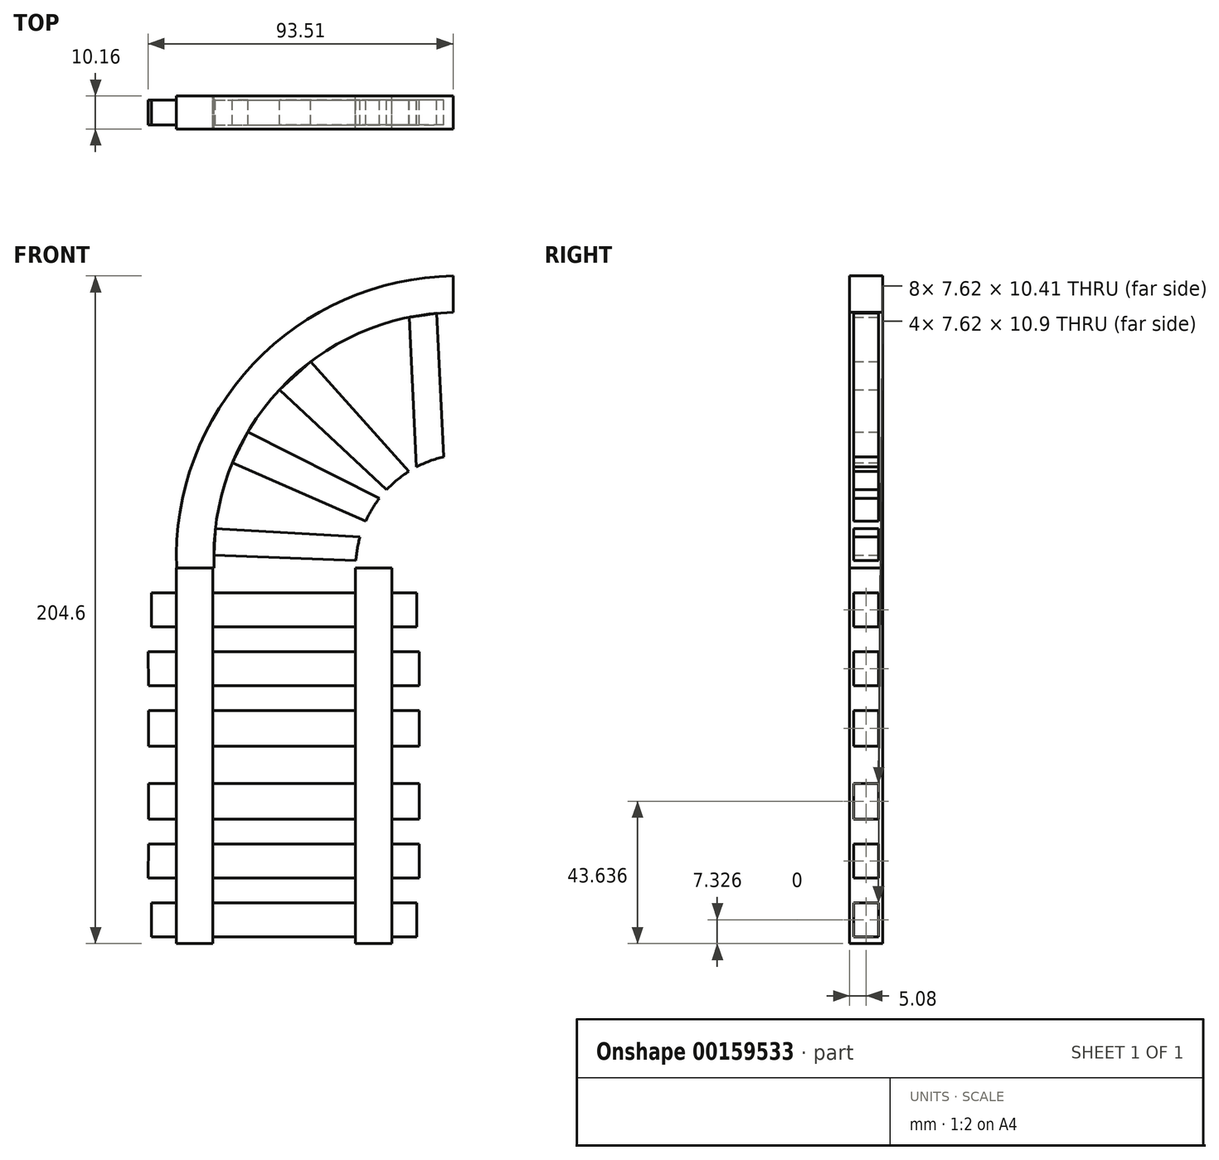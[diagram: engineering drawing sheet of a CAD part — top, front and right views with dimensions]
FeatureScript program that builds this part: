
annotation { "Feature Type Name" : "Feature", "Feature Type Description" : "" }
export const myFeature = defineFeature(function(context is Context, id is Id, definition is map)
    precondition{}
    {
        {
            var Q0;
            Q0=qCreatedBy(makeId("Front.planeOp"),FACE);
            var sketch = newSketch(context, id + "F0", { "sketchPlane" : qUnion([Q0])});
            skLineSegment(sketch, "E0", {"start": v(-21.84, 60.28) * mm, "end": v(-21.84, -54.78) * mm});
            skLineSegment(sketch, "E1", {"start": v(-21.84, -54.78) * mm, "end": v(-33.02, -54.78) * mm});
            skLineSegment(sketch, "E2", {"start": v(-33.02, -54.78) * mm, "end": v(-33.02, 60.28) * mm});
            skLineSegment(sketch, "E3", {"start": v(-33.02, 60.28) * mm, "end": v(-21.84, 60.28) * mm});
            skLineSegment(sketch, "E4.MirrorCS", {"start": v(21.84, 60.28) * mm, "end": v(21.84, -54.78) * mm});
            skLineSegment(sketch, "E5.MirrorCS", {"start": v(33.02, -54.78) * mm, "end": v(33.02, 60.28) * mm});
            skLineSegment(sketch, "E6.MirrorCS", {"start": v(33.02, 60.28) * mm, "end": v(21.84, 60.28) * mm});
            skLineSegment(sketch, "E7.MirrorCS", {"start": v(21.84, -54.78) * mm, "end": v(33.02, -54.78) * mm});
            skLineSegment(sketch, "E8", {"start": v(-40.64, 42.25) * mm, "end": v(40.64, 42.25) * mm});
            skLineSegment(sketch, "E9", {"start": v(40.64, 42.25) * mm, "end": v(40.64, 52.66) * mm});
            skLineSegment(sketch, "E10", {"start": v(40.64, 52.66) * mm, "end": v(-40.64, 52.66) * mm});
            skLineSegment(sketch, "E11", {"start": v(-40.64, 52.66) * mm, "end": v(-40.64, 42.25) * mm});
            skLineSegment(sketch, "E12", {"start": v(-41.74, 34.63) * mm, "end": v(41.35, 34.63) * mm});
            skLineSegment(sketch, "E13", {"start": v(41.35, 34.63) * mm, "end": v(41.35, 24.21) * mm});
            skLineSegment(sketch, "E14", {"start": v(41.35, 24.21) * mm, "end": v(-41.51, 24.21) * mm});
            skLineSegment(sketch, "E15", {"start": v(-41.51, 24.21) * mm, "end": v(-41.74, 34.63) * mm});
            skLineSegment(sketch, "E16", {"start": v(-33.02, 16.6) * mm, "end": v(-41.51, 16.6) * mm});
            skLineSegment(sketch, "E17", {"start": v(-41.51, 16.6) * mm, "end": v(-41.51, 5.7) * mm});
            skLineSegment(sketch, "E18", {"start": v(-41.51, 5.7) * mm, "end": v(41.4, 5.7) * mm});
            skLineSegment(sketch, "E19", {"start": v(41.4, 5.7) * mm, "end": v(41.4, 16.6) * mm});
            skLineSegment(sketch, "E20", {"start": v(-33.02, 16.6) * mm, "end": v(41.4, 16.6) * mm});
            skLineSegment(sketch, "E21.MirrorCS", {"start": v(-41.51, -5.7) * mm, "end": v(41.4, -5.7) * mm});
            skLineSegment(sketch, "E22.MirrorCS", {"start": v(-41.51, -16.6) * mm, "end": v(-41.51, -5.7) * mm});
            skLineSegment(sketch, "E23.MirrorCS", {"start": v(41.4, -5.7) * mm, "end": v(41.4, -16.6) * mm});
            skLineSegment(sketch, "E24.MirrorCS", {"start": v(-33.02, -16.6) * mm, "end": v(41.4, -16.6) * mm});
            skLineSegment(sketch, "E25.MirrorCS", {"start": v(-33.02, -16.6) * mm, "end": v(-41.51, -16.6) * mm});
            skLineSegment(sketch, "E26.MirrorCS", {"start": v(41.35, -24.21) * mm, "end": v(-41.51, -24.21) * mm});
            skLineSegment(sketch, "E27.MirrorCS", {"start": v(-41.74, -34.63) * mm, "end": v(41.35, -34.63) * mm});
            skLineSegment(sketch, "E28.MirrorCS", {"start": v(-41.51, -24.21) * mm, "end": v(-41.74, -34.63) * mm});
            skLineSegment(sketch, "E29.MirrorCS", {"start": v(41.35, -34.63) * mm, "end": v(41.35, -24.21) * mm});
            skLineSegment(sketch, "E30.MirrorCS", {"start": v(40.64, -42.25) * mm, "end": v(40.64, -52.66) * mm});
            skLineSegment(sketch, "E31.MirrorCS", {"start": v(40.64, -52.66) * mm, "end": v(-40.64, -52.66) * mm});
            skLineSegment(sketch, "E32.MirrorCS", {"start": v(-40.64, -42.25) * mm, "end": v(40.64, -42.25) * mm});
            skLineSegment(sketch, "E33.MirrorCS", {"start": v(-40.64, -52.66) * mm, "end": v(-40.64, -42.25) * mm});
            skSolve(sketch);
        }
        {
            var Q0;
            {var subQ0=sQuery(id+"F0.wireOp",EDGE,"E3");Q0=makeQuery(id+"F0.imprint","IMPRINT",FACE,{"disambiguationData":[TD([[makeQuery(id+"F0.imprint","IMPRINT",EDGE,{"derivedFrom":subQ0}),-1.0]])]});}
            var Q1;
            {var subQ0=sQuery(id+"F0.wireOp",EDGE,"E10");var subQ1=sQuery(id+"F0.wireOp",EDGE,"E0");var subQ2=makeQuery(id+"F0.imprint","INTERSECT",VERTEX,{"derivedFrom":[subQ1,subQ0]});Q1=makeQuery(id+"F0.imprint","IMPRINT",FACE,{"disambiguationData":[TD([[makeQuery(id+"F0.imprint","IMPRINT",EDGE,{"disambiguationData":[TD([[subQ2,-1.0]])],"derivedFrom":subQ1}),-1.0]])]});}
            var Q2;
            {var subQ0=sQuery(id+"F0.wireOp",EDGE,"E8");var subQ1=sQuery(id+"F0.wireOp",EDGE,"E0");var subQ2=makeQuery(id+"F0.imprint","INTERSECT",VERTEX,{"derivedFrom":[subQ1,subQ0]});Q2=makeQuery(id+"F0.imprint","IMPRINT",FACE,{"disambiguationData":[TD([[makeQuery(id+"F0.imprint","IMPRINT",EDGE,{"disambiguationData":[TD([[subQ2,-1.0]])],"derivedFrom":subQ1}),-1.0]])]});}
            var Q3;
            {var subQ0=sQuery(id+"F0.wireOp",EDGE,"E12");var subQ1=sQuery(id+"F0.wireOp",EDGE,"E0");var subQ2=makeQuery(id+"F0.imprint","INTERSECT",VERTEX,{"derivedFrom":[subQ1,subQ0]});Q3=makeQuery(id+"F0.imprint","IMPRINT",FACE,{"disambiguationData":[TD([[makeQuery(id+"F0.imprint","IMPRINT",EDGE,{"disambiguationData":[TD([[subQ2,-1.0]])],"derivedFrom":subQ1}),-1.0]])]});}
            var Q4;
            {var subQ0=sQuery(id+"F0.wireOp",EDGE,"E14");var subQ1=sQuery(id+"F0.wireOp",EDGE,"E0");var subQ2=makeQuery(id+"F0.imprint","INTERSECT",VERTEX,{"derivedFrom":[subQ1,subQ0]});Q4=makeQuery(id+"F0.imprint","IMPRINT",FACE,{"disambiguationData":[TD([[makeQuery(id+"F0.imprint","IMPRINT",EDGE,{"disambiguationData":[TD([[subQ2,-1.0]])],"derivedFrom":subQ1}),-1.0]])]});}
            var Q5;
            {var subQ0=sQuery(id+"F0.wireOp",EDGE,"E20");var subQ1=sQuery(id+"F0.wireOp",EDGE,"E0");var subQ2=makeQuery(id+"F0.imprint","INTERSECT",VERTEX,{"derivedFrom":[subQ1,subQ0]});Q5=makeQuery(id+"F0.imprint","IMPRINT",FACE,{"disambiguationData":[TD([[makeQuery(id+"F0.imprint","IMPRINT",EDGE,{"disambiguationData":[TD([[subQ2,-1.0]])],"derivedFrom":subQ1}),-1.0]])]});}
            var Q6;
            {var subQ0=sQuery(id+"F0.wireOp",EDGE,"E18");var subQ1=sQuery(id+"F0.wireOp",EDGE,"E0");var subQ2=makeQuery(id+"F0.imprint","INTERSECT",VERTEX,{"derivedFrom":[subQ1,subQ0]});Q6=makeQuery(id+"F0.imprint","IMPRINT",FACE,{"disambiguationData":[TD([[makeQuery(id+"F0.imprint","IMPRINT",EDGE,{"disambiguationData":[TD([[subQ2,-1.0]])],"derivedFrom":subQ1}),-1.0]])]});}
            var Q7;
            {var subQ0=sQuery(id+"F0.wireOp",EDGE,"E21.MirrorCS");var subQ1=sQuery(id+"F0.wireOp",EDGE,"E0");var subQ2=makeQuery(id+"F0.imprint","INTERSECT",VERTEX,{"derivedFrom":[subQ1,subQ0]});Q7=makeQuery(id+"F0.imprint","IMPRINT",FACE,{"disambiguationData":[TD([[makeQuery(id+"F0.imprint","IMPRINT",EDGE,{"disambiguationData":[TD([[subQ2,-1.0]])],"derivedFrom":subQ1}),-1.0]])]});}
            var Q8;
            {var subQ0=sQuery(id+"F0.wireOp",EDGE,"E24.MirrorCS");var subQ1=sQuery(id+"F0.wireOp",EDGE,"E0");var subQ2=makeQuery(id+"F0.imprint","INTERSECT",VERTEX,{"derivedFrom":[subQ1,subQ0]});Q8=makeQuery(id+"F0.imprint","IMPRINT",FACE,{"disambiguationData":[TD([[makeQuery(id+"F0.imprint","IMPRINT",EDGE,{"disambiguationData":[TD([[subQ2,-1.0]])],"derivedFrom":subQ1}),-1.0]])]});}
            var Q9;
            {var subQ0=sQuery(id+"F0.wireOp",EDGE,"E26.MirrorCS");var subQ1=sQuery(id+"F0.wireOp",EDGE,"E0");var subQ2=makeQuery(id+"F0.imprint","INTERSECT",VERTEX,{"derivedFrom":[subQ1,subQ0]});Q9=makeQuery(id+"F0.imprint","IMPRINT",FACE,{"disambiguationData":[TD([[makeQuery(id+"F0.imprint","IMPRINT",EDGE,{"disambiguationData":[TD([[subQ2,-1.0]])],"derivedFrom":subQ1}),-1.0]])]});}
            var Q10;
            {var subQ0=sQuery(id+"F0.wireOp",EDGE,"E27.MirrorCS");var subQ1=sQuery(id+"F0.wireOp",EDGE,"E0");var subQ2=makeQuery(id+"F0.imprint","INTERSECT",VERTEX,{"derivedFrom":[subQ1,subQ0]});Q10=makeQuery(id+"F0.imprint","IMPRINT",FACE,{"disambiguationData":[TD([[makeQuery(id+"F0.imprint","IMPRINT",EDGE,{"disambiguationData":[TD([[subQ2,-1.0]])],"derivedFrom":subQ1}),-1.0]])]});}
            var Q11;
            {var subQ0=sQuery(id+"F0.wireOp",EDGE,"E31.MirrorCS");var subQ1=sQuery(id+"F0.wireOp",EDGE,"E0");var subQ2=makeQuery(id+"F0.imprint","INTERSECT",VERTEX,{"derivedFrom":[subQ1,subQ0]});Q11=makeQuery(id+"F0.imprint","IMPRINT",FACE,{"disambiguationData":[TD([[makeQuery(id+"F0.imprint","IMPRINT",EDGE,{"disambiguationData":[TD([[subQ2,1.0]])],"derivedFrom":subQ1}),-1.0]])]});}
            var Q12;
            {var subQ0=sQuery(id+"F0.wireOp",EDGE,"E31.MirrorCS");var subQ1=sQuery(id+"F0.wireOp",EDGE,"E4.MirrorCS");var subQ2=makeQuery(id+"F0.imprint","INTERSECT",VERTEX,{"derivedFrom":[subQ1,subQ0]});Q12=makeQuery(id+"F0.imprint","IMPRINT",FACE,{"disambiguationData":[TD([[makeQuery(id+"F0.imprint","IMPRINT",EDGE,{"disambiguationData":[TD([[subQ2,1.0]])],"derivedFrom":subQ1}),1.0]])]});}
            var Q13;
            {var subQ0=sQuery(id+"F0.wireOp",EDGE,"E27.MirrorCS");var subQ1=sQuery(id+"F0.wireOp",EDGE,"E4.MirrorCS");var subQ2=makeQuery(id+"F0.imprint","INTERSECT",VERTEX,{"derivedFrom":[subQ1,subQ0]});Q13=makeQuery(id+"F0.imprint","IMPRINT",FACE,{"disambiguationData":[TD([[makeQuery(id+"F0.imprint","IMPRINT",EDGE,{"disambiguationData":[TD([[subQ2,-1.0]])],"derivedFrom":subQ1}),1.0]])]});}
            var Q14;
            {var subQ0=sQuery(id+"F0.wireOp",EDGE,"E26.MirrorCS");var subQ1=sQuery(id+"F0.wireOp",EDGE,"E4.MirrorCS");var subQ2=makeQuery(id+"F0.imprint","INTERSECT",VERTEX,{"derivedFrom":[subQ1,subQ0]});Q14=makeQuery(id+"F0.imprint","IMPRINT",FACE,{"disambiguationData":[TD([[makeQuery(id+"F0.imprint","IMPRINT",EDGE,{"disambiguationData":[TD([[subQ2,-1.0]])],"derivedFrom":subQ1}),1.0]])]});}
            var Q15;
            {var subQ0=sQuery(id+"F0.wireOp",EDGE,"E24.MirrorCS");var subQ1=sQuery(id+"F0.wireOp",EDGE,"E4.MirrorCS");var subQ2=makeQuery(id+"F0.imprint","INTERSECT",VERTEX,{"derivedFrom":[subQ1,subQ0]});Q15=makeQuery(id+"F0.imprint","IMPRINT",FACE,{"disambiguationData":[TD([[makeQuery(id+"F0.imprint","IMPRINT",EDGE,{"disambiguationData":[TD([[subQ2,-1.0]])],"derivedFrom":subQ1}),1.0]])]});}
            var Q16;
            {var subQ0=sQuery(id+"F0.wireOp",EDGE,"E21.MirrorCS");var subQ1=sQuery(id+"F0.wireOp",EDGE,"E4.MirrorCS");var subQ2=makeQuery(id+"F0.imprint","INTERSECT",VERTEX,{"derivedFrom":[subQ1,subQ0]});Q16=makeQuery(id+"F0.imprint","IMPRINT",FACE,{"disambiguationData":[TD([[makeQuery(id+"F0.imprint","IMPRINT",EDGE,{"disambiguationData":[TD([[subQ2,-1.0]])],"derivedFrom":subQ1}),1.0]])]});}
            var Q17;
            {var subQ0=sQuery(id+"F0.wireOp",EDGE,"E18");var subQ1=sQuery(id+"F0.wireOp",EDGE,"E4.MirrorCS");var subQ2=makeQuery(id+"F0.imprint","INTERSECT",VERTEX,{"derivedFrom":[subQ1,subQ0]});Q17=makeQuery(id+"F0.imprint","IMPRINT",FACE,{"disambiguationData":[TD([[makeQuery(id+"F0.imprint","IMPRINT",EDGE,{"disambiguationData":[TD([[subQ2,-1.0]])],"derivedFrom":subQ1}),1.0]])]});}
            var Q18;
            {var subQ0=sQuery(id+"F0.wireOp",EDGE,"E20");var subQ1=sQuery(id+"F0.wireOp",EDGE,"E4.MirrorCS");var subQ2=makeQuery(id+"F0.imprint","INTERSECT",VERTEX,{"derivedFrom":[subQ1,subQ0]});Q18=makeQuery(id+"F0.imprint","IMPRINT",FACE,{"disambiguationData":[TD([[makeQuery(id+"F0.imprint","IMPRINT",EDGE,{"disambiguationData":[TD([[subQ2,-1.0]])],"derivedFrom":subQ1}),1.0]])]});}
            var Q19;
            {var subQ0=sQuery(id+"F0.wireOp",EDGE,"E14");var subQ1=sQuery(id+"F0.wireOp",EDGE,"E4.MirrorCS");var subQ2=makeQuery(id+"F0.imprint","INTERSECT",VERTEX,{"derivedFrom":[subQ1,subQ0]});Q19=makeQuery(id+"F0.imprint","IMPRINT",FACE,{"disambiguationData":[TD([[makeQuery(id+"F0.imprint","IMPRINT",EDGE,{"disambiguationData":[TD([[subQ2,-1.0]])],"derivedFrom":subQ1}),1.0]])]});}
            var Q20;
            {var subQ0=sQuery(id+"F0.wireOp",EDGE,"E12");var subQ1=sQuery(id+"F0.wireOp",EDGE,"E4.MirrorCS");var subQ2=makeQuery(id+"F0.imprint","INTERSECT",VERTEX,{"derivedFrom":[subQ1,subQ0]});Q20=makeQuery(id+"F0.imprint","IMPRINT",FACE,{"disambiguationData":[TD([[makeQuery(id+"F0.imprint","IMPRINT",EDGE,{"disambiguationData":[TD([[subQ2,-1.0]])],"derivedFrom":subQ1}),1.0]])]});}
            var Q21;
            {var subQ0=sQuery(id+"F0.wireOp",EDGE,"E8");var subQ1=sQuery(id+"F0.wireOp",EDGE,"E4.MirrorCS");var subQ2=makeQuery(id+"F0.imprint","INTERSECT",VERTEX,{"derivedFrom":[subQ1,subQ0]});Q21=makeQuery(id+"F0.imprint","IMPRINT",FACE,{"disambiguationData":[TD([[makeQuery(id+"F0.imprint","IMPRINT",EDGE,{"disambiguationData":[TD([[subQ2,-1.0]])],"derivedFrom":subQ1}),1.0]])]});}
            var Q22;
            {var subQ0=sQuery(id+"F0.wireOp",EDGE,"E10");var subQ1=sQuery(id+"F0.wireOp",EDGE,"E4.MirrorCS");var subQ2=makeQuery(id+"F0.imprint","INTERSECT",VERTEX,{"derivedFrom":[subQ1,subQ0]});Q22=makeQuery(id+"F0.imprint","IMPRINT",FACE,{"disambiguationData":[TD([[makeQuery(id+"F0.imprint","IMPRINT",EDGE,{"disambiguationData":[TD([[subQ2,-1.0]])],"derivedFrom":subQ1}),1.0]])]});}
            var Q23;
            {var subQ0=sQuery(id+"F0.wireOp",EDGE,"E6.MirrorCS");Q23=makeQuery(id+"F0.imprint","IMPRINT",FACE,{"disambiguationData":[TD([[makeQuery(id+"F0.imprint","IMPRINT",EDGE,{"derivedFrom":subQ0}),1.0]])]});}
            var Q24;
            {var subQ0=sQuery(id+"F0.wireOp",EDGE,"E7.MirrorCS");Q24=makeQuery(id+"F0.imprint","IMPRINT",FACE,{"disambiguationData":[TD([[makeQuery(id+"F0.imprint","IMPRINT",EDGE,{"derivedFrom":subQ0}),1.0]])]});}
            var Q25;
            {var subQ0=sQuery(id+"F0.wireOp",EDGE,"E1");Q25=makeQuery(id+"F0.imprint","IMPRINT",FACE,{"disambiguationData":[TD([[makeQuery(id+"F0.imprint","IMPRINT",EDGE,{"derivedFrom":subQ0}),-1.0]])]});}
            extrude(context, id + "F1", {"entities" : qUnion([Q0, Q1, Q2, Q3, Q4, Q5, Q6, Q7, Q8, Q9, Q10, Q11, Q12, Q13, Q14, Q15, Q16, Q17, Q18, Q19, Q20, Q21, Q22, Q23, Q24, Q25]), "depth" : 5.08 * mm, "hasSecondDirection" : true, "secondDirectionOppositeDirection" : true, "secondDirectionDepth" : 5.08 * mm});
        }
        {
            var Q0;
            {var subQ0=sQuery(id+"F0.wireOp",EDGE,"E12");var subQ1=sQuery(id+"F0.wireOp",EDGE,"E0");var subQ2=makeQuery(id+"F0.imprint","INTERSECT",VERTEX,{"derivedFrom":[subQ1,subQ0]});Q0=makeQuery(id+"F0.imprint","IMPRINT",FACE,{"disambiguationData":[TD([[makeQuery(id+"F0.imprint","IMPRINT",EDGE,{"disambiguationData":[TD([[subQ2,-1.0]])],"derivedFrom":subQ1}),1.0]])]});}
            var Q1;
            {var subQ0=sQuery(id+"F0.wireOp",EDGE,"E10");var subQ1=sQuery(id+"F0.wireOp",EDGE,"E0");var subQ2=makeQuery(id+"F0.imprint","INTERSECT",VERTEX,{"derivedFrom":[subQ1,subQ0]});Q1=makeQuery(id+"F0.imprint","IMPRINT",FACE,{"disambiguationData":[TD([[makeQuery(id+"F0.imprint","IMPRINT",EDGE,{"disambiguationData":[TD([[subQ2,-1.0]])],"derivedFrom":subQ1}),1.0]])]});}
            var Q2;
            {var subQ5=sQuery(id+"F0.wireOp",EDGE,"E11");Q2=makeQuery(id+"F0.imprint","IMPRINT",FACE,{"disambiguationData":[TD([[makeQuery(id+"F0.imprint","IMPRINT",EDGE,{"derivedFrom":subQ5}),1.0]])]});}
            var Q3;
            {var subQ5=sQuery(id+"F0.wireOp",EDGE,"E15");Q3=makeQuery(id+"F0.imprint","IMPRINT",FACE,{"disambiguationData":[TD([[makeQuery(id+"F0.imprint","IMPRINT",EDGE,{"derivedFrom":subQ5}),-1.0]])]});}
            var Q4;
            {var subQ0=sQuery(id+"F0.wireOp",EDGE,"E16");Q4=makeQuery(id+"F0.imprint","IMPRINT",FACE,{"disambiguationData":[TD([[makeQuery(id+"F0.imprint","IMPRINT",EDGE,{"derivedFrom":subQ0}),1.0]])]});}
            var Q5;
            {var subQ4=sQuery(id+"F0.wireOp",EDGE,"E22.MirrorCS");Q5=makeQuery(id+"F0.imprint","IMPRINT",FACE,{"disambiguationData":[TD([[makeQuery(id+"F0.imprint","IMPRINT",EDGE,{"derivedFrom":subQ4}),-1.0]])]});}
            var Q6;
            {var subQ0=sQuery(id+"F0.wireOp",EDGE,"E21.MirrorCS");var subQ1=sQuery(id+"F0.wireOp",EDGE,"E0");var subQ2=makeQuery(id+"F0.imprint","INTERSECT",VERTEX,{"derivedFrom":[subQ1,subQ0]});Q6=makeQuery(id+"F0.imprint","IMPRINT",FACE,{"disambiguationData":[TD([[makeQuery(id+"F0.imprint","IMPRINT",EDGE,{"disambiguationData":[TD([[subQ2,-1.0]])],"derivedFrom":subQ1}),1.0]])]});}
            var Q7;
            {var subQ0=sQuery(id+"F0.wireOp",EDGE,"E20");var subQ1=sQuery(id+"F0.wireOp",EDGE,"E0");var subQ2=makeQuery(id+"F0.imprint","INTERSECT",VERTEX,{"derivedFrom":[subQ1,subQ0]});Q7=makeQuery(id+"F0.imprint","IMPRINT",FACE,{"disambiguationData":[TD([[makeQuery(id+"F0.imprint","IMPRINT",EDGE,{"disambiguationData":[TD([[subQ2,-1.0]])],"derivedFrom":subQ1}),1.0]])]});}
            var Q8;
            {var subQ0=sQuery(id+"F0.wireOp",EDGE,"E24.MirrorCS");var subQ1=sQuery(id+"F0.wireOp",EDGE,"E5.MirrorCS");var subQ2=makeQuery(id+"F0.imprint","INTERSECT",VERTEX,{"derivedFrom":[subQ1,subQ0]});Q8=makeQuery(id+"F0.imprint","IMPRINT",FACE,{"disambiguationData":[TD([[makeQuery(id+"F0.imprint","IMPRINT",EDGE,{"disambiguationData":[TD([[subQ2,-1.0]])],"derivedFrom":subQ1}),-1.0]])]});}
            var Q9;
            {var subQ0=sQuery(id+"F0.wireOp",EDGE,"E18");var subQ1=sQuery(id+"F0.wireOp",EDGE,"E5.MirrorCS");var subQ2=makeQuery(id+"F0.imprint","INTERSECT",VERTEX,{"derivedFrom":[subQ1,subQ0]});Q9=makeQuery(id+"F0.imprint","IMPRINT",FACE,{"disambiguationData":[TD([[makeQuery(id+"F0.imprint","IMPRINT",EDGE,{"disambiguationData":[TD([[subQ2,-1.0]])],"derivedFrom":subQ1}),-1.0]])]});}
            var Q10;
            {var subQ5=sQuery(id+"F0.wireOp",EDGE,"E13");Q10=makeQuery(id+"F0.imprint","IMPRINT",FACE,{"disambiguationData":[TD([[makeQuery(id+"F0.imprint","IMPRINT",EDGE,{"derivedFrom":subQ5}),-1.0]])]});}
            var Q11;
            {var subQ5=sQuery(id+"F0.wireOp",EDGE,"E9");Q11=makeQuery(id+"F0.imprint","IMPRINT",FACE,{"disambiguationData":[TD([[makeQuery(id+"F0.imprint","IMPRINT",EDGE,{"derivedFrom":subQ5}),1.0]])]});}
            var Q12;
            {var subQ5=sQuery(id+"F0.wireOp",EDGE,"E29.MirrorCS");Q12=makeQuery(id+"F0.imprint","IMPRINT",FACE,{"disambiguationData":[TD([[makeQuery(id+"F0.imprint","IMPRINT",EDGE,{"derivedFrom":subQ5}),1.0]])]});}
            var Q13;
            {var subQ5=sQuery(id+"F0.wireOp",EDGE,"E30.MirrorCS");Q13=makeQuery(id+"F0.imprint","IMPRINT",FACE,{"disambiguationData":[TD([[makeQuery(id+"F0.imprint","IMPRINT",EDGE,{"derivedFrom":subQ5}),-1.0]])]});}
            var Q14;
            {var subQ0=sQuery(id+"F0.wireOp",EDGE,"E31.MirrorCS");var subQ1=sQuery(id+"F0.wireOp",EDGE,"E0");var subQ2=makeQuery(id+"F0.imprint","INTERSECT",VERTEX,{"derivedFrom":[subQ1,subQ0]});Q14=makeQuery(id+"F0.imprint","IMPRINT",FACE,{"disambiguationData":[TD([[makeQuery(id+"F0.imprint","IMPRINT",EDGE,{"disambiguationData":[TD([[subQ2,1.0]])],"derivedFrom":subQ1}),1.0]])]});}
            var Q15;
            {var subQ0=sQuery(id+"F0.wireOp",EDGE,"E26.MirrorCS");var subQ1=sQuery(id+"F0.wireOp",EDGE,"E0");var subQ2=makeQuery(id+"F0.imprint","INTERSECT",VERTEX,{"derivedFrom":[subQ1,subQ0]});Q15=makeQuery(id+"F0.imprint","IMPRINT",FACE,{"disambiguationData":[TD([[makeQuery(id+"F0.imprint","IMPRINT",EDGE,{"disambiguationData":[TD([[subQ2,-1.0]])],"derivedFrom":subQ1}),1.0]])]});}
            var Q16;
            {var subQ5=sQuery(id+"F0.wireOp",EDGE,"E28.MirrorCS");Q16=makeQuery(id+"F0.imprint","IMPRINT",FACE,{"disambiguationData":[TD([[makeQuery(id+"F0.imprint","IMPRINT",EDGE,{"derivedFrom":subQ5}),1.0]])]});}
            var Q17;
            {var subQ5=sQuery(id+"F0.wireOp",EDGE,"E33.MirrorCS");Q17=makeQuery(id+"F0.imprint","IMPRINT",FACE,{"disambiguationData":[TD([[makeQuery(id+"F0.imprint","IMPRINT",EDGE,{"derivedFrom":subQ5}),-1.0]])]});}
            var Q18;
            Q18=qSketchRegion(id+"F3",true);
            extrude(context, id + "F2", {"entities" : qUnion([Q0, Q1, Q2, Q3, Q4, Q5, Q6, Q7, Q8, Q9, Q10, Q11, Q12, Q13, Q14, Q15, Q16, Q17, Q18]), "operationType" : NewBodyOperationType.ADD, "depth" : 3.8 * mm, "hasSecondDirection" : true, "secondDirectionOppositeDirection" : true, "secondDirectionDepth" : 3.8 * mm});
        }
        {
            var Q0;
            Q0=qCreatedBy(makeId("Front.planeOp"),FACE);
            var sketch = newSketch(context, id + "F3", { "sketchPlane" : qUnion([Q0])});
            skLineSegment(sketch, "E34", {"start": v(51.77, 83.78) * mm, "end": v(51.77, 149.82) * mm});
            skArc(sketch, "E35", {"start": v(51.77, 149.82) * mm, "mid": v(-9.44, 122.88) * mm, "end": v(-32.96, 60.28) * mm});
            skLineSegment(sketch, "E36", {"start": v(51.77, 149.82) * mm, "end": v(51.77, 138.64) * mm});
            skLineSegment(sketch, "E37", {"start": v(51.77, 83.78) * mm, "end": v(51.77, 94.95) * mm});
            skArc(sketch, "E38", {"start": v(51.77, 138.64) * mm, "mid": v(-1.44, 114.97) * mm, "end": v(-21.43, 60.28) * mm});
            skArc(sketch, "E39", {"start": v(51.77, 83.78) * mm, "mid": v(37.26, 76.12) * mm, "end": v(33.02, 60.28) * mm});
            skArc(sketch, "E40", {"start": v(51.77, 94.95) * mm, "mid": v(25, 74.7) * mm, "end": v(27.58, 41.24) * mm});
            skLineSegment(sketch, "E41", {"start": v(-21.52, 64.26) * mm, "end": v(21.98, 62.59) * mm});
            skLineSegment(sketch, "E42", {"start": v(-21.06, 72.4) * mm, "end": v(23.24, 69.9) * mm});
            skLineSegment(sketch, "E43", {"start": v(-15.86, 92.57) * mm, "end": v(25, 74.7) * mm});
            skLineSegment(sketch, "E44", {"start": v(-11.13, 102.04) * mm, "end": v(29.15, 81.66) * mm});
            skLineSegment(sketch, "E45", {"start": v(33.02, 60.28) * mm, "end": v(21.9, 60.28) * mm});
            skLineSegment(sketch, "E46", {"start": v(-21.43, 60.28) * mm, "end": v(-32.96, 60.28) * mm});
            skLineSegment(sketch, "E47", {"start": v(48.84, 94.4) * mm, "end": v(46.72, 138.38) * mm});
            skLineSegment(sketch, "E48", {"start": v(31.4, 84.31) * mm, "end": v(-1.44, 114.97) * mm});
            skLineSegment(sketch, "E49", {"start": v(8.07, 123.54) * mm, "end": v(38.2, 89.91) * mm});
            skLineSegment(sketch, "E50", {"start": v(40.54, 91.27) * mm, "end": v(38.33, 137.18) * mm});
            skLineSegment(sketch, "E51", {"start": v(21.98, 62.59) * mm, "end": v(23.24, 69.9) * mm});
            skLineSegment(sketch, "E52", {"start": v(-21.06, 72.4) * mm, "end": v(-21.52, 64.26) * mm});
            skLineSegment(sketch, "E53", {"start": v(-11.13, 102.04) * mm, "end": v(-15.86, 92.57) * mm});
            skLineSegment(sketch, "E54", {"start": v(29.15, 81.66) * mm, "end": v(25, 74.7) * mm});
            skLineSegment(sketch, "E55", {"start": v(31.4, 84.31) * mm, "end": v(38.2, 89.91) * mm});
            skLineSegment(sketch, "E56", {"start": v(8.07, 123.54) * mm, "end": v(-1.44, 114.97) * mm});
            skLineSegment(sketch, "E57", {"start": v(38.33, 137.18) * mm, "end": v(46.72, 138.38) * mm});
            skLineSegment(sketch, "E58", {"start": v(40.54, 91.27) * mm, "end": v(48.84, 94.4) * mm});
            skSolve(sketch);
        }
        {
            var Q0;
            Q0=makeQuery(id+"F3.imprint","IMPRINT",FACE,{"disambiguationData":[TD([[makeQuery(id+"F3.imprint","IMPRINT",EDGE,{"derivedFrom":sQuery(id+"F3.wireOp",EDGE,"E35")}),1.0]])]});
            var Q1;
            {var subQ5=sQuery(id+"F3.wireOp",EDGE,"E37");Q1=makeQuery(id+"F3.imprint","IMPRINT",FACE,{"disambiguationData":[TD([[makeQuery(id+"F3.imprint","IMPRINT",EDGE,{"derivedFrom":subQ5}),1.0]])]});}
            extrude(context, id + "F4", {"entities" : qUnion([Q0, Q1]), "depth" : 5.08 * mm, "hasSecondDirection" : true, "secondDirectionOppositeDirection" : true, "secondDirectionDepth" : 5.08 * mm});
        }
        {
            var Q0;
            {var subQ1=sQuery(id+"F3.wireOp",EDGE,"E41");Q0=makeQuery(id+"F3.imprint","IMPRINT",FACE,{"disambiguationData":[TD([[makeQuery(id+"F3.imprint","IMPRINT",EDGE,{"derivedFrom":subQ1}),1.0]])]});}
            var Q1;
            {var subQ1=sQuery(id+"F3.wireOp",EDGE,"E43");Q1=makeQuery(id+"F3.imprint","IMPRINT",FACE,{"disambiguationData":[TD([[makeQuery(id+"F3.imprint","IMPRINT",EDGE,{"derivedFrom":subQ1}),1.0]])]});}
            var Q2;
            {var subQ1=sQuery(id+"F3.wireOp",EDGE,"E48");Q2=makeQuery(id+"F3.imprint","IMPRINT",FACE,{"disambiguationData":[TD([[makeQuery(id+"F3.imprint","IMPRINT",EDGE,{"derivedFrom":subQ1}),-1.0]])]});}
            var Q3;
            {var subQ1=sQuery(id+"F3.wireOp",EDGE,"E47");Q3=makeQuery(id+"F3.imprint","IMPRINT",FACE,{"disambiguationData":[TD([[makeQuery(id+"F3.imprint","IMPRINT",EDGE,{"derivedFrom":subQ1}),1.0]])]});}
            extrude(context, id + "F5", {"entities" : qUnion([Q0, Q1, Q2, Q3]), "operationType" : NewBodyOperationType.ADD, "depth" : 3.8 * mm, "hasSecondDirection" : true, "secondDirectionOppositeDirection" : true, "secondDirectionDepth" : 3.8 * mm});
        }
    });
